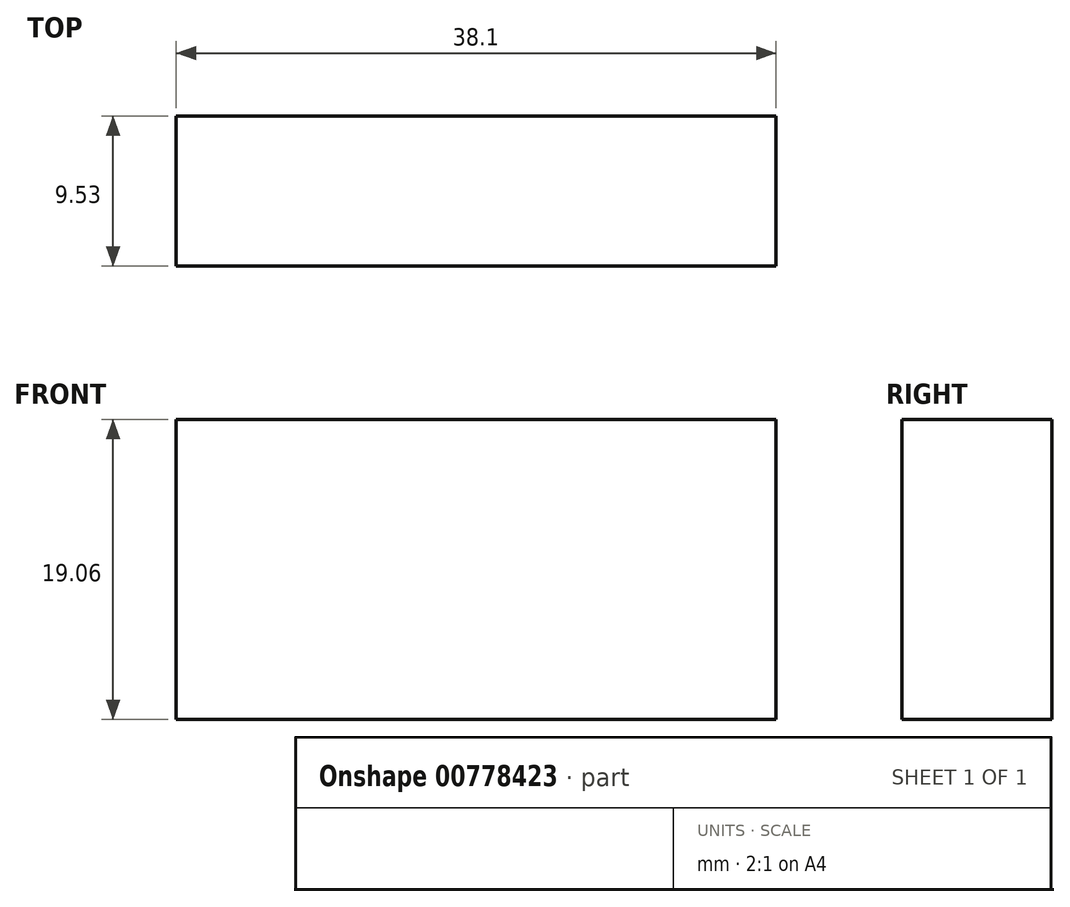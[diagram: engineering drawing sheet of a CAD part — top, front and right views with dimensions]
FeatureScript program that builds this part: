
annotation { "Feature Type Name" : "Feature", "Feature Type Description" : "" }
export const myFeature = defineFeature(function(context is Context, id is Id, definition is map)
    precondition{}
    {
        {
            var Q0;
            Q0=qCreatedBy(makeId("Front.planeOp"),FACE);
            var sketch = newSketch(context, id + "F0", { "sketchPlane" : qUnion([Q0])});
            skLineSegment(sketch, "E0.bottom", {"start": v(19.05, -9.52) * mm, "end": v(-19.05, -9.53) * mm});
            skLineSegment(sketch, "E0.top", {"start": v(19.05, 9.53) * mm, "end": v(-19.05, 9.53) * mm});
            skLineSegment(sketch, "E0.left", {"start": v(19.05, -9.52) * mm, "end": v(19.05, 9.53) * mm});
            skLineSegment(sketch, "E0.right", {"start": v(-19.05, -9.53) * mm, "end": v(-19.05, 9.53) * mm});
            skPoint(sketch, "E0.middle", {"position": v(0, 0) * mm});
            skSolve(sketch);
        }
        {
            var Q0;
            Q0=makeQuery(id+"F0.imprint","IMPRINT",FACE,{"disambiguationData":[TD([[makeQuery(id+"F0.imprint","IMPRINT",EDGE,{"derivedFrom":sQuery(id+"F0.wireOp",EDGE,"E0.bottom")}),-1.0]])]});
            extrude(context, id + "F1", {"entities" : qUnion([Q0]), "depth" : 9.52 * mm, "offsetDistance" : 25.4 * mm});
        }
    });
